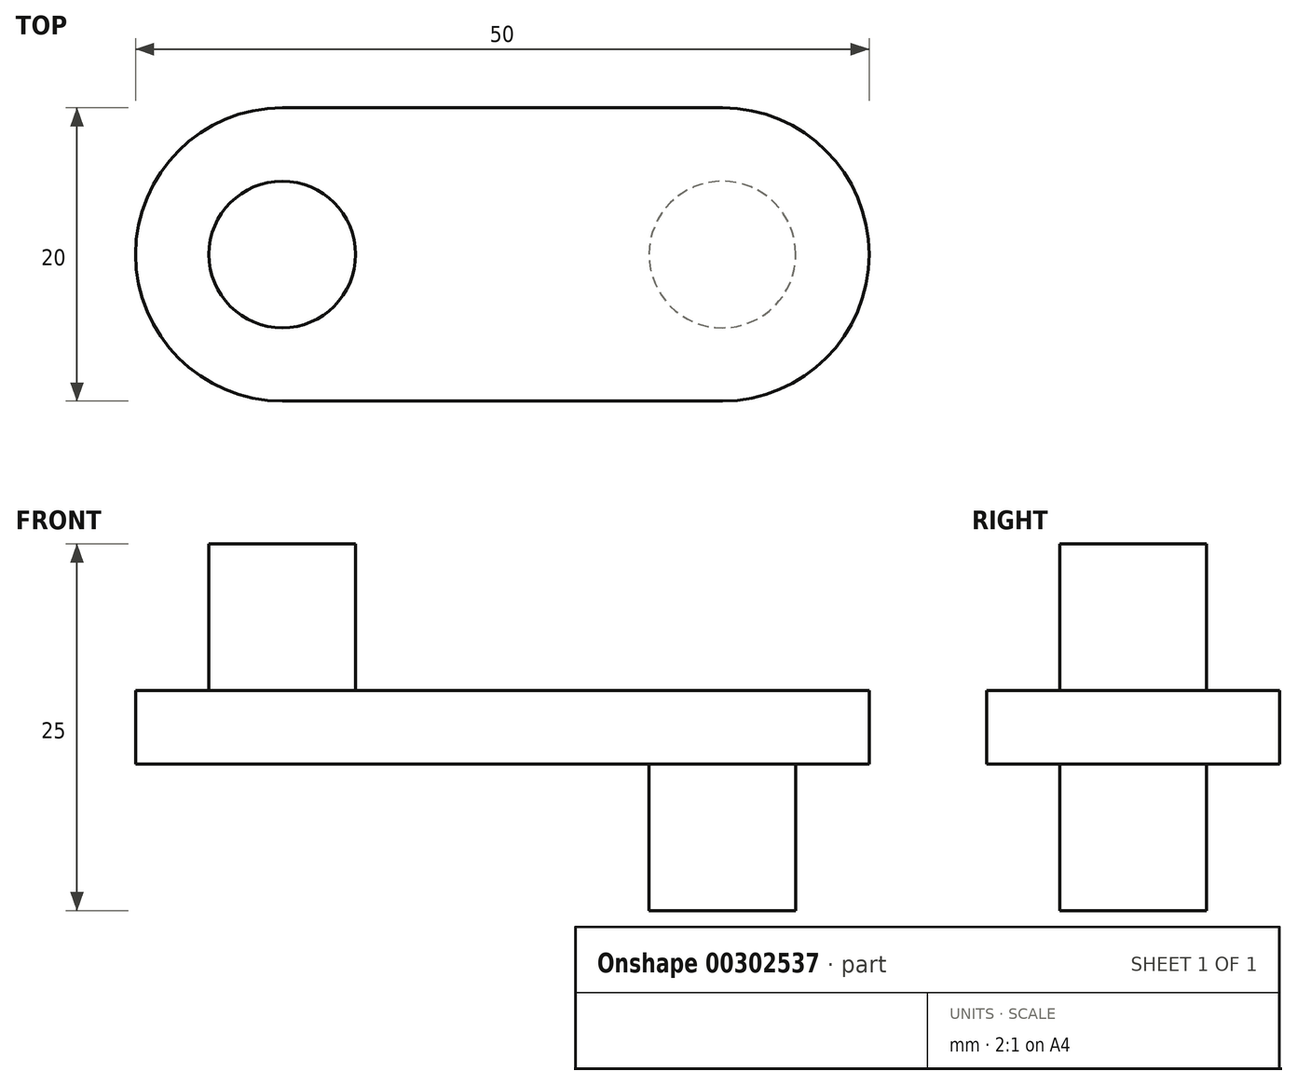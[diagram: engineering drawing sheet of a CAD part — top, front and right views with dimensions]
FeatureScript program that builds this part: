
annotation { "Feature Type Name" : "Feature", "Feature Type Description" : "" }
export const myFeature = defineFeature(function(context is Context, id is Id, definition is map)
    precondition{}
    {
        {
            var Q0;
            Q0=qCreatedBy(makeId("Top.planeOp"),FACE);
            var sketch = newSketch(context, id + "F0", { "sketchPlane" : qUnion([Q0])});
            skLineSegment(sketch, "E0", {"start": v(-15, 0) * mm, "end": v(15, 0) * mm});
            skLineSegment(sketch, "E1", {"start": v(-15, -20) * mm, "end": v(15, -20) * mm});
            skArc(sketch, "E2", {"start": v(15, -20) * mm, "mid": v(25, -10) * mm, "end": v(15, 0) * mm});
            skArc(sketch, "E3", {"start": v(-15, 0) * mm, "mid": v(-25, -10) * mm, "end": v(-15, -20) * mm});
            skLineSegment(sketch, "E4", {"start": v(15, 0) * mm, "end": v(15, -20) * mm, "construction": true});
            skLineSegment(sketch, "E5", {"start": v(-15, 0) * mm, "end": v(-15, -24.03) * mm, "construction": true});
            skCircle(sketch, "E6", {"center": v(-15, -10) * mm, "radius": 5 * mm});
            skCircle(sketch, "E7", {"center": v(15, -10) * mm, "radius": 5 * mm});
            skSolve(sketch);
        }
        {
            var Q0;
            Q0=makeQuery(id+"F0.imprint","IMPRINT",FACE,{"disambiguationData":[TD([[makeQuery(id+"F0.imprint","IMPRINT",EDGE,{"derivedFrom":sQuery(id+"F0.wireOp",EDGE,"E0")}),-1.0]])]});
            extrude(context, id + "F1", {"entities" : qUnion([Q0]), "depth" : 5 * mm});
        }
        {
            var Q0;
            Q0=makeQuery(id+"F0.imprint","IMPRINT",FACE,{"disambiguationData":[TD([[makeQuery(id+"F0.imprint","IMPRINT",EDGE,{"derivedFrom":sQuery(id+"F0.wireOp",EDGE,"E6")}),1.0]])]});
            extrude(context, id + "F2", {"entities" : qUnion([Q0]), "operationType" : NewBodyOperationType.ADD, "depth" : 15 * mm});
        }
        {
            var Q0;
            Q0=makeQuery(id+"F0.imprint","IMPRINT",FACE,{"disambiguationData":[TD([[makeQuery(id+"F0.imprint","IMPRINT",EDGE,{"derivedFrom":sQuery(id+"F0.wireOp",EDGE,"E7")}),1.0]])]});
            var Q1;
            Q1=makeQuery(id+"F1.opExtrude","CAP_FACE",FACE,{"disambiguationData":[OSD([sQuery(id+"F0.wireOp",EDGE,"E0"),sQuery(id+"F0.wireOp",EDGE,"E1"),sQuery(id+"F0.wireOp",EDGE,"E2"),sQuery(id+"F0.wireOp",EDGE,"E3"),sQuery(id+"F0.wireOp",EDGE,"E6"),sQuery(id+"F0.wireOp",EDGE,"E7")])],"isStart":false});
            extrude(context, id + "F3", {"entities" : qUnion([Q0]), "operationType" : NewBodyOperationType.ADD, "oppositeDirection" : true, "depth" : 10 * mm, "hasSecondDirection" : true, "secondDirectionBound" : SecondDirectionBoundingType.UP_TO_SURFACE, "secondDirectionOppositeDirection" : false, "secondDirectionBoundEntityFace" : qUnion([Q1]), "secondDirectionDepth" : 25 * mm});
        }
    });
